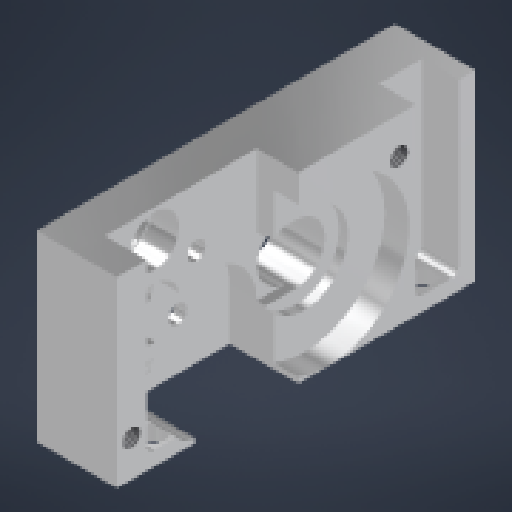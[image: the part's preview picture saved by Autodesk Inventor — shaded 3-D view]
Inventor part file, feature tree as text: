
AUTODESK INVENTOR PART (.ipt)
format: ipt  version: 2023 (Build 270158000, 158)  size: 473,600 bytes
history: native  units: mm
features: sketch x10, hole x9, extrude x7, fillet x2, projected_geometry x2, other x1
ambient origin geometry x8: Origin, YZ Plane, XZ Plane, XY Plane, X Axis, Y Axis, Z Axis, Center Point
bodies: Body1 (feature_tree)
feature tree (31):
  other  "Bryła1"
  extrude  "Wyciągnięcie proste1"  Depth=2.5mm
  sketch  "Szkic2"
  extrude  "Wyciągnięcie proste2"  Depth=10.0mm
  hole  "Otwór1"  [1 undecoded]
  hole  "Otwór2"  [1 undecoded]
  hole  "Otwór3"  [1 undecoded]
  hole  "Otwór4"  [1 undecoded]
  hole  "Otwór5"  [1 undecoded]
  hole  "Otwór6"  [1 undecoded]
  hole  "Otwór7"  [1 undecoded]
  extrude  "Wyciągnięcie proste3"  TaperAngle=0.0deg  [1 undecoded]
  hole  "Otwór9"  [1 undecoded]
  hole  "Otwór10"  [1 undecoded]
  fillet  "Zaokrąglenie1"  [1 undecoded]
  extrude  "Wyciągnięcie proste4"  Depth=5.0mm TaperAngle=0.0deg
  extrude  "Wyciągnięcie proste7"  Depth=2.0mm
  fillet  "Zaokrąglenie2"  Radius=5.9mm
  extrude  "Extrusion8"  Depth=10.0mm
  extrude  "Extrusion9"  Depth=11.0mm
  sketch  "Szkic1"
  sketch  "Szkic3"
  sketch  "Szkic4"
  sketch  "Szkic6"
  sketch  "Szkic7"
  sketch  "Szkic8"
  projected_geometry  "Pętla rzutowana2"
  sketch  "Szkic13"
  projected_geometry  "Pętla rzutowana3"
  sketch  "Sketch14"  dims[d3=0.0mm d4=2.5mm]
  sketch  "Sketch15"  dims[d5=7.0mm d8=10.8mm d10=13.75mm d11=28.9mm d13=11.170107mm d14=7.0mm d15=0.0mm d16=8.1mm d17=6.0mm d18=4.0mm d19=2.0mm d20=90.0deg d21=8.0mm d22=20.594885mm d24=6.0mm d25=4.0mm d26=2.0mm d27=90.0deg d29=0.0mm d31=6.0mm d32=4.0mm d33=2.0mm d34=90.0deg d36=0.0mm d37=8.5mm d38=6.8mm d39=6.0mm d40=4.0mm d41=2.0mm d42=90.0deg d43=9.5mm d44=0.0mm d45=3.4mm d46=6.0mm d47=6.3mm d48=2.0mm d49=90.0deg d50=5.2mm d51=0.0mm d53=2.0mm d56=2.459mm d57=8.0mm d58=6.3mm d59=2.0mm d60=90.0deg d61=6.0mm d62=20.594885mm d63=22.0mm d64=6.0mm d65=11.5mm d66=2.0mm d67=90.0deg d69=0.0mm d83=5.0mm d84=0.0mm d85=2.0mm d86=5.9mm d87=12.5mm d88=11.0mm d89=7.0mm d90=4.0mm d91=5.0mm d92=17.0mm d93=2.459mm d94=6.0mm d95=4.0mm d96=2.0mm d97=90.0deg d98=7.0mm d99=20.594885mm d100=3.2mm d101=6.0mm d102=6.3mm d103=2.0mm d104=90.0deg d105=7.0mm d106=20.594885mm d107=5.25mm d108=5.0mm d109=10.5mm d110=1.0mm d111=10.0mm d112=0.0mm d113=5.0mm d120=10.0mm d121=0.0mm d122=7.0mm d123=12.0mm d124=1.2mm d125=0.0mm d126=10.0mm d127=0.0mm]
note: 11 required parameter values undecoded (feature->parameter linkage not recoverable at this tier; creation-order binding heuristic only, values carry confidence <= 0.55)
